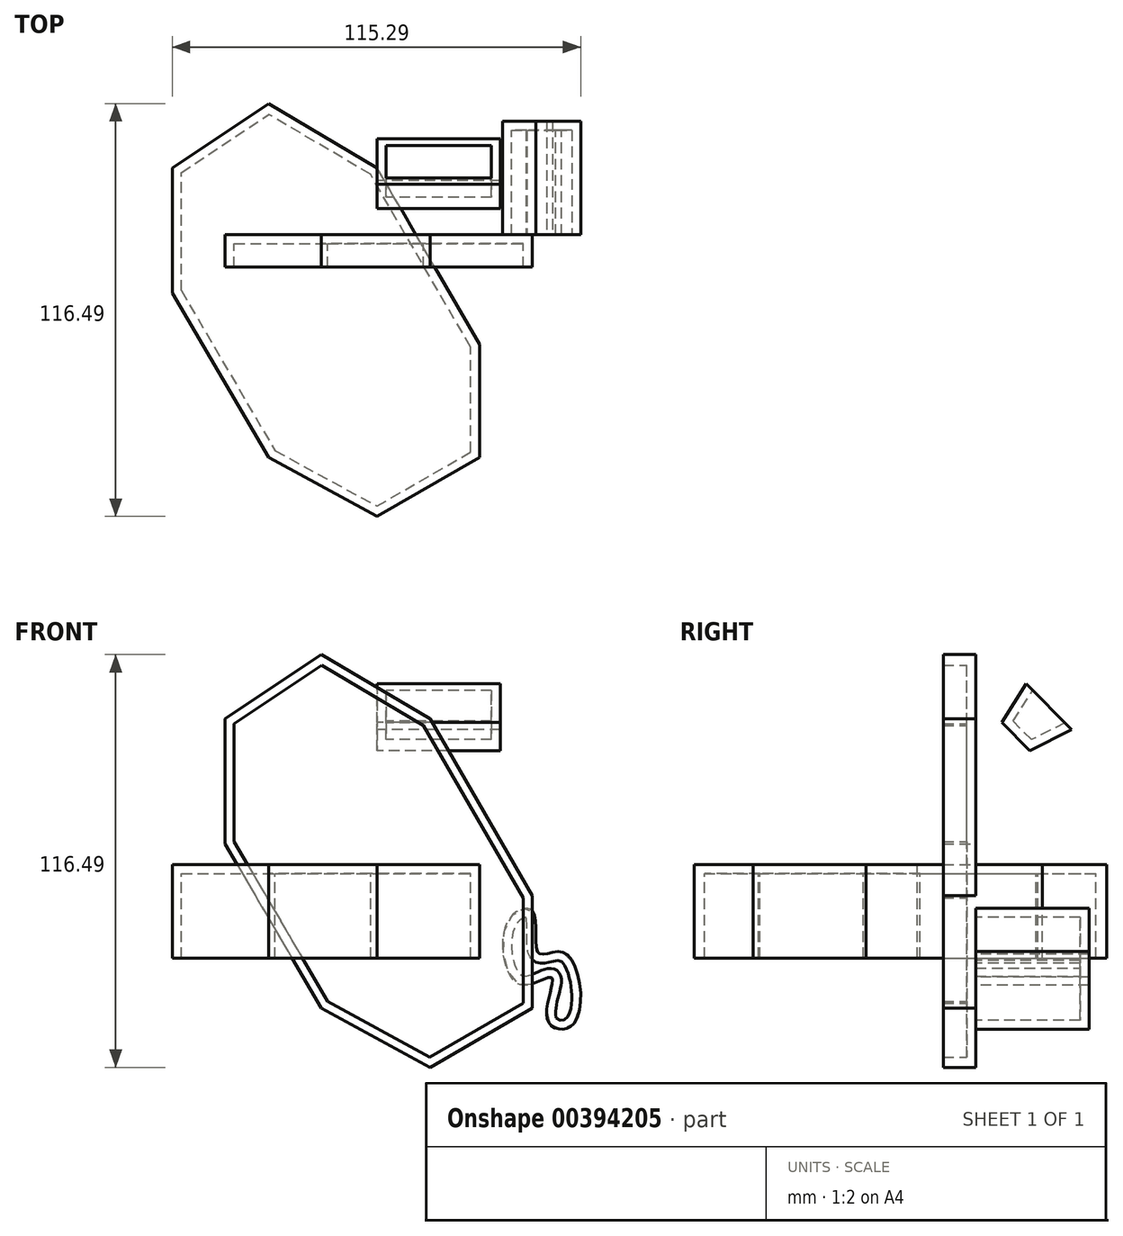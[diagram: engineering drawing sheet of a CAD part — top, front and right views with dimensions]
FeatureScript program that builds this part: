
annotation { "Feature Type Name" : "Feature", "Feature Type Description" : "" }
export const myFeature = defineFeature(function(context is Context, id is Id, definition is map)
    precondition{}
    {
        {
            var Q0;
            Q0=qCreatedBy(makeId("Top.planeOp"),FACE);
            var sketch = newSketch(context, id + "F0", { "sketchPlane" : qUnion([Q0])});
            skLineSegment(sketch, "E0", {"start": v(-57.82, -16.46) * mm, "end": v(-30.7, -62.84) * mm});
            skLineSegment(sketch, "E1", {"start": v(-30.7, -62.84) * mm, "end": v(0, -79.5) * mm});
            skLineSegment(sketch, "E2", {"start": v(0, -79.5) * mm, "end": v(28.88, -62.84) * mm});
            skLineSegment(sketch, "E3", {"start": v(28.88, -62.84) * mm, "end": v(28.88, -31.01) * mm});
            skLineSegment(sketch, "E4", {"start": v(28.88, -31.01) * mm, "end": v(0, 18.85) * mm});
            skLineSegment(sketch, "E5", {"start": v(0, 18.85) * mm, "end": v(-30.7, 36.98) * mm});
            skLineSegment(sketch, "E6", {"start": v(-57.82, -16.46) * mm, "end": v(-57.82, 18.85) * mm});
            skLineSegment(sketch, "E7", {"start": v(-57.82, 18.85) * mm, "end": v(-30.7, 36.98) * mm});
            skSolve(sketch);
        }
        {
            var Q0;
            Q0=qCreatedBy(makeId("Right.planeOp"),FACE);
            var sketch = newSketch(context, id + "F1", { "sketchPlane" : qUnion([Q0])});
            skLineSegment(sketch, "E8", {"start": v(14.23, 51.04) * mm, "end": v(27.04, 38.03) * mm});
            skLineSegment(sketch, "E9", {"start": v(27.04, 38.03) * mm, "end": v(15.22, 32.12) * mm});
            skLineSegment(sketch, "E10", {"start": v(15.22, 32.12) * mm, "end": v(7.4, 40.07) * mm});
            skLineSegment(sketch, "E11", {"start": v(7.4, 40.07) * mm, "end": v(14.23, 51.04) * mm});
            skSolve(sketch);
        }
        {
            var Q0;
            Q0 = qSketchRegion(id + "F0", true);
            extrude(context, id + "F2", {"entities" : qUnion([Q0]), "oppositeDirection" : true, "depth" : 26.42 * mm});
        }
        {
            var Q0;
            Q0=makeQuery(id+"F2.opExtrude","CAP_FACE",FACE,{"disambiguationData":[OSD([sQuery(id+"F0.wireOp",EDGE,"E0"),sQuery(id+"F0.wireOp",EDGE,"E1"),sQuery(id+"F0.wireOp",EDGE,"E2"),sQuery(id+"F0.wireOp",EDGE,"E3"),sQuery(id+"F0.wireOp",EDGE,"E4"),sQuery(id+"F0.wireOp",EDGE,"E5"),sQuery(id+"F0.wireOp",EDGE,"E6"),sQuery(id+"F0.wireOp",EDGE,"E7")])],"isStart":false});
            shell(context, id + "F3", {"entities" : qUnion([Q0]), "thickness" : 2.54 * mm});
        }
        {
            var Q0;
            Q0=makeQuery(id+"F1.imprint","IMPRINT",FACE,{"disambiguationData":[TD([[makeQuery(id+"F1.imprint","IMPRINT",EDGE,{"derivedFrom":sQuery(id+"F1.wireOp",EDGE,"E8")}),-1.0]])]});
            extrude(context, id + "F4", {"entities" : qUnion([Q0]), "depth" : 34.8 * mm});
        }
        {
            var Q0;
            Q0=makeQuery(id+"F4.opExtrude","SWEPT_FACE",FACE,{"disambiguationData":[OSD([sQuery(id+"F1.wireOp",EDGE,"E8")])]});
            shell(context, id + "F5", {"entities" : qUnion([Q0]), "thickness" : 2.54 * mm});
        }
        {
            var Q0;
            Q0=qCreatedBy(makeId("Front.planeOp"),FACE);
            var sketch = newSketch(context, id + "F6", { "sketchPlane" : qUnion([Q0])});
            skFitSpline(sketch, "E12", {"points": [v(55.58, -44.8) * mm, v(53.02, -25.02) * mm, v(45.53, -25.02) * mm, v(43.96, -13.31) * mm, v(36.67, -16.38) * mm, v(40.4, -33.93) * mm, v(49.28, -31.98) * mm, v(48.1, -43.97) * mm, v(55.58, -44.8) * mm]});
            skSolve(sketch);
        }
        {
            var Q0;
            Q0=makeQuery(id+"F6.imprint","IMPRINT",FACE,{"disambiguationData":[TD([[makeQuery(id+"F6.imprint","IMPRINT",EDGE,{"derivedFrom":sQuery(id+"F6.wireOp",EDGE,"E12")}),1.0]])]});
            extrude(context, id + "F7", {"entities" : qUnion([Q0]), "oppositeDirection" : true, "depth" : 32 * mm});
        }
        {
            var Q0;
            Q0=makeQuery(id+"F7.opExtrude","CAP_FACE",FACE,{"disambiguationData":[OSD([sQuery(id+"F6.wireOp",EDGE,"E12")])],"isStart":true});
            shell(context, id + "F8", {"entities" : qUnion([Q0]), "thickness" : 2.54 * mm});
        }
        {
            var Q0;
            Q0=qCreatedBy(makeId("Front.planeOp"),FACE);
            var sketch = newSketch(context, id + "F9", { "sketchPlane" : qUnion([Q0])});
            skLineSegment(sketch, "E13", {"start": v(-42.91, 5.78) * mm, "end": v(-15.79, -40.6) * mm});
            skLineSegment(sketch, "E14", {"start": v(-15.79, -40.6) * mm, "end": v(14.9, -57.26) * mm});
            skLineSegment(sketch, "E15", {"start": v(14.9, -57.26) * mm, "end": v(43.8, -40.6) * mm});
            skLineSegment(sketch, "E16", {"start": v(43.8, -40.6) * mm, "end": v(43.8, -8.76) * mm});
            skLineSegment(sketch, "E17", {"start": v(43.8, -8.76) * mm, "end": v(14.9, 41.1) * mm});
            skLineSegment(sketch, "E18", {"start": v(14.9, 41.1) * mm, "end": v(-15.79, 59.23) * mm});
            skLineSegment(sketch, "E19", {"start": v(-42.91, 5.78) * mm, "end": v(-42.91, 41.1) * mm});
            skLineSegment(sketch, "E20", {"start": v(-42.91, 41.1) * mm, "end": v(-15.79, 59.23) * mm});
            skSolve(sketch);
        }
        {
            var Q0;
            Q0 = qSketchRegion(id + "F9", true);
            extrude(context, id + "F10", {"entities" : qUnion([Q0]), "depth" : 9.14 * mm});
        }
        {
            var Q0;
            Q0=makeQuery(id+"F10.opExtrude","CAP_FACE",FACE,{"disambiguationData":[OSD([sQuery(id+"F9.wireOp",EDGE,"E13"),sQuery(id+"F9.wireOp",EDGE,"E14"),sQuery(id+"F9.wireOp",EDGE,"E15"),sQuery(id+"F9.wireOp",EDGE,"E16"),sQuery(id+"F9.wireOp",EDGE,"E17"),sQuery(id+"F9.wireOp",EDGE,"E18"),sQuery(id+"F9.wireOp",EDGE,"E19"),sQuery(id+"F9.wireOp",EDGE,"E20")])],"isStart":false});
            shell(context, id + "F11", {"entities" : qUnion([Q0]), "thickness" : 2.54 * mm});
        }
    });
